# Revit family: Tinka 7W
name_source: partatom
category: Lighting Fixtures
revit_build: Autodesk Revit 2018 (Build: 20170525_2315(x64)
units: mm (PartAtom-declared; Revit-internal decimal feet)

## family parameters
Cut with Voids When Loaded = No
Host = Face
Light Source = No
OmniClass Number = 23.80.70.11.14.21
OmniClass Title = Spots and Tracklight Specialties
Part Type = Normal
Room Calculation Point = No
Round Connector Dimension = Use Diameter
Shared = No

## types (2) — shared parameters
Beam Angle = 30°
CRI = 82
Casing Color = White
Cutout = -
Default Elevation = 1219 mm
Depth = -
Description = Tracklight, 3-Circuit Track
Dimensions = 72mm x 225mm
Dimmable = Yes
Directivity = Yes
Driver = Integrated
Housing Material = Aluminium
IP Code = IP20
Lamp = LED
Last Updated = 2.3.2017
Lifetime L70 = 50000h
Manufacturer = Winled Oy Ltd
Model = Tinka 7W
Operating Temperature Range = -20° to +50°C
Type Image = Tinka 7W.png
URL = www.winled.fi
Voltage = 230 V
Wattage Comments = 7W

## per-type parameters (varying)
| type | Color Temperature | Light Source | Lumens Output | Product Number |
| Tinka 7W, Neutral White, 230V - 53ER997N007E | 4000K | Tinka light NV | 602lm | 53ER997N015E |
| Tinka 7W, Warm White, 230V - 53ER997L007E | 3000K | Tinka light LV | 562lm | 53ER997L015E |

## geometry (parser evidence)
native form markers: Sweep x19
no freeform markers — native parametric forms only
